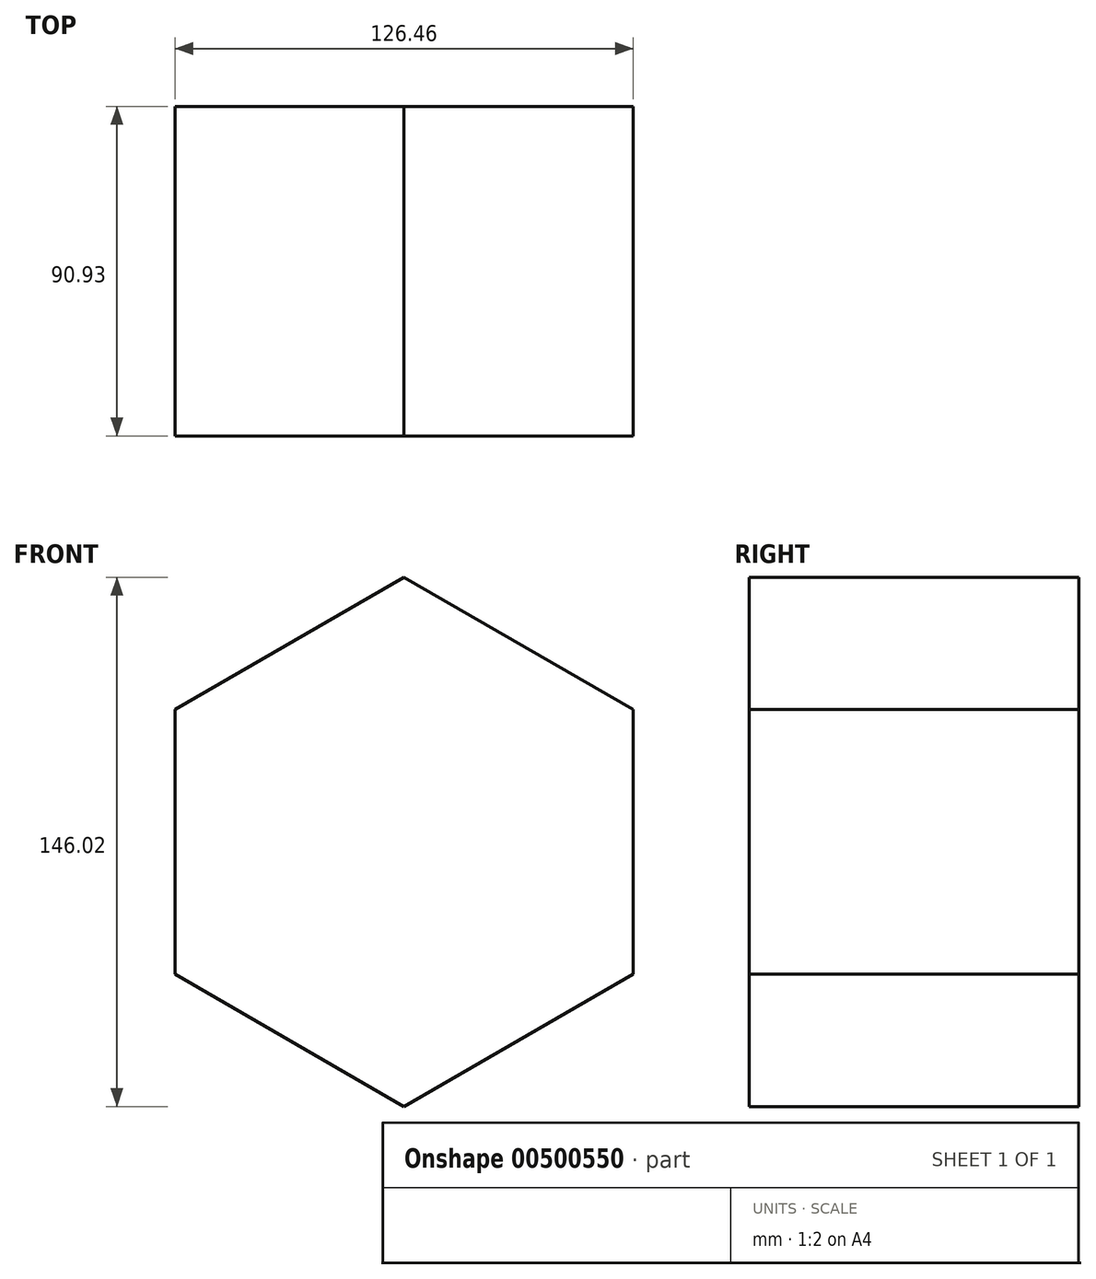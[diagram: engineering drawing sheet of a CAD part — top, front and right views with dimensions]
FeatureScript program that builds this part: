
annotation { "Feature Type Name" : "Feature", "Feature Type Description" : "" }
export const myFeature = defineFeature(function(context is Context, id is Id, definition is map)
    precondition{}
    {
        {
            var Q0;
            Q0=qCreatedBy(makeId("Front.planeOp"),FACE);
            var sketch = newSketch(context, id + "F0", { "sketchPlane" : qUnion([Q0])});
            skCircle(sketch, "E0.cCircle", {"center": v(0, 0) * mm, "radius": 73.01 * mm, "construction": true});
            skLineSegment(sketch, "E0.0", {"start": v(0, 73.01) * mm, "end": v(63.23, 36.5) * mm});
            skLineSegment(sketch, "E0.1", {"start": v(63.23, 36.5) * mm, "end": v(63.23, -36.5) * mm});
            skLineSegment(sketch, "E0.2", {"start": v(63.23, -36.5) * mm, "end": v(0, -73.01) * mm});
            skLineSegment(sketch, "E0.3", {"start": v(0, -73.01) * mm, "end": v(-63.23, -36.5) * mm});
            skLineSegment(sketch, "E0.4", {"start": v(-63.23, -36.5) * mm, "end": v(-63.23, 36.5) * mm});
            skLineSegment(sketch, "E0.5", {"start": v(-63.23, 36.5) * mm, "end": v(0, 73.01) * mm});
            skSolve(sketch);
        }
        {
            var Q0;
            Q0=makeQuery(id+"F0.imprint","IMPRINT",FACE,{"disambiguationData":[TD([[makeQuery(id+"F0.imprint","IMPRINT",EDGE,{"derivedFrom":sQuery(id+"F0.wireOp",EDGE,"E0.0")}),-1.0]])]});
            extrude(context, id + "F1", {"entities" : qUnion([Q0]), "depth" : 90.93 * mm});
        }
    });
